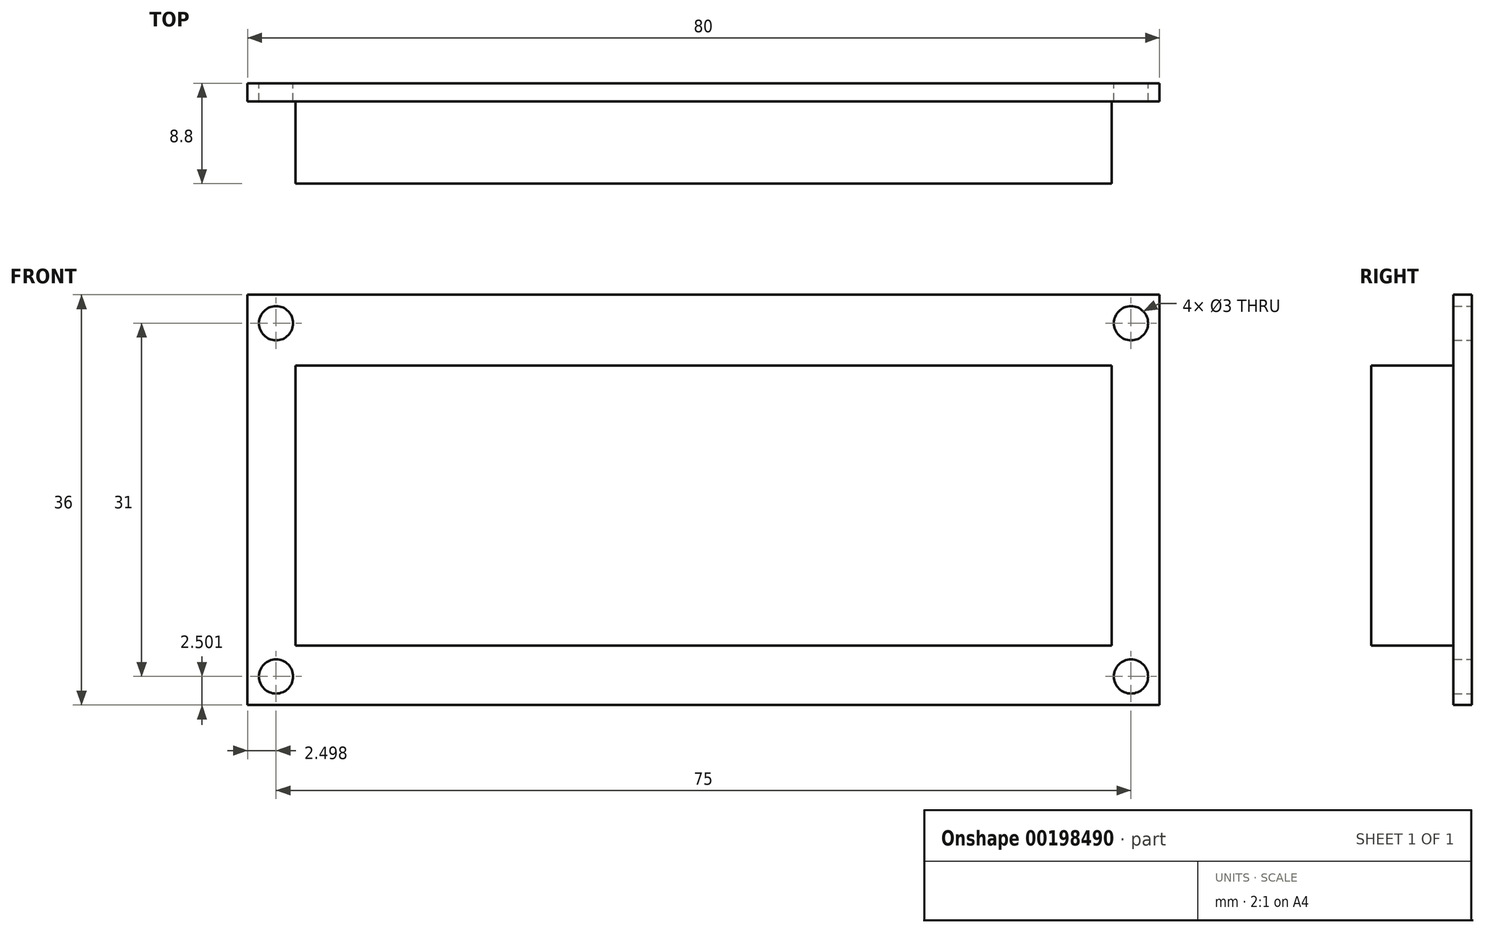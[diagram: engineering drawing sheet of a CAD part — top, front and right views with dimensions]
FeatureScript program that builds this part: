
annotation { "Feature Type Name" : "Feature", "Feature Type Description" : "" }
export const myFeature = defineFeature(function(context is Context, id is Id, definition is map)
    precondition{}
    {
        {
            var Q0;
            Q0=qCreatedBy(makeId("Front.planeOp"),FACE);
            var sketch = newSketch(context, id + "F0", { "sketchPlane" : qUnion([Q0])});
            skLineSegment(sketch, "E0.bottom", {"start": v(-37.3, 13.68) * mm, "end": v(42.7, 13.68) * mm});
            skLineSegment(sketch, "E0.top", {"start": v(-37.3, -22.32) * mm, "end": v(42.7, -22.32) * mm});
            skLineSegment(sketch, "E0.left", {"start": v(-37.3, 13.68) * mm, "end": v(-37.3, -22.32) * mm});
            skLineSegment(sketch, "E0.right", {"start": v(42.7, 13.68) * mm, "end": v(42.7, -22.32) * mm});
            skCircle(sketch, "E1", {"center": v(-34.8, 11.18) * mm, "radius": 1.5 * mm});
            skCircle(sketch, "E2", {"center": v(40.2, 11.18) * mm, "radius": 1.5 * mm});
            skCircle(sketch, "E3", {"center": v(40.2, -19.82) * mm, "radius": 1.5 * mm});
            skCircle(sketch, "E4", {"center": v(-34.8, -19.82) * mm, "radius": 1.5 * mm});
            skSolve(sketch);
        }
        {
            var Q0;
            Q0=makeQuery(id+"F0.imprint","IMPRINT",FACE,{"disambiguationData":[TD([[makeQuery(id+"F0.imprint","IMPRINT",EDGE,{"derivedFrom":sQuery(id+"F0.wireOp",EDGE,"E0.bottom")}),-1.0]])]});
            extrude(context, id + "F1", {"entities" : qUnion([Q0]), "depth" : 1.6 * mm});
        }
        {
            var Q0;
            Q0=makeQuery(id+"F1.opExtrude","CAP_FACE",FACE,{"disambiguationData":[OSD([sQuery(id+"F0.wireOp",EDGE,"E0.bottom"),sQuery(id+"F0.wireOp",EDGE,"E0.top"),sQuery(id+"F0.wireOp",EDGE,"E0.left"),sQuery(id+"F0.wireOp",EDGE,"E0.right"),sQuery(id+"F0.wireOp",EDGE,"E1"),sQuery(id+"F0.wireOp",EDGE,"E2"),sQuery(id+"F0.wireOp",EDGE,"E3"),sQuery(id+"F0.wireOp",EDGE,"E4")])],"isStart":false});
            var sketch = newSketch(context, id + "F2", { "sketchPlane" : qUnion([Q0])});
            skLineSegment(sketch, "E5.bottom", {"start": v(-33.1, 7.48) * mm, "end": v(38.5, 7.48) * mm});
            skLineSegment(sketch, "E5.top", {"start": v(-33.1, -17.12) * mm, "end": v(38.5, -17.12) * mm});
            skLineSegment(sketch, "E5.left", {"start": v(-33.1, 7.48) * mm, "end": v(-33.1, -17.12) * mm});
            skLineSegment(sketch, "E5.right", {"start": v(38.5, 7.48) * mm, "end": v(38.5, -17.12) * mm});
            skSolve(sketch);
        }
        {
            var Q0;
            Q0 = qSketchRegion(id + "F2", true);
            extrude(context, id + "F3", {"entities" : qUnion([Q0]), "operationType" : NewBodyOperationType.ADD, "depth" : 7.2 * mm});
        }
        {
            var Q0;
            Q0=makeQuery(id+"F3.opExtrude","CAP_FACE",FACE,{"disambiguationData":[OSD([sQuery(id+"F2.wireOp",EDGE,"E5.bottom"),sQuery(id+"F2.wireOp",EDGE,"E5.top"),sQuery(id+"F2.wireOp",EDGE,"E5.left"),sQuery(id+"F2.wireOp",EDGE,"E5.right")])],"isStart":false});
            var sketch = newSketch(context, id + "F4", { "sketchPlane" : qUnion([Q0])});
            skLineSegment(sketch, "E6.bottom", {"start": v(-29.75, 1.53) * mm, "end": v(35.25, 1.53) * mm});
            skLineSegment(sketch, "E6.top", {"start": v(-29.75, -12.47) * mm, "end": v(35.25, -12.47) * mm});
            skLineSegment(sketch, "E6.left", {"start": v(-29.75, 1.53) * mm, "end": v(-29.75, -12.47) * mm});
            skLineSegment(sketch, "E6.right", {"start": v(35.25, 1.53) * mm, "end": v(35.25, -12.47) * mm});
            skSolve(sketch);
        }
        {
            var Q0;
            Q0=makeQuery(id+"F4.imprint","IMPRINT",FACE,{"disambiguationData":[TD([[makeQuery(id+"F4.imprint","IMPRINT",EDGE,{"derivedFrom":sQuery(id+"F4.wireOp",EDGE,"E6.bottom")}),-1.0]])]});
            extrude(context, id + "F5", {"entities" : qUnion([Q0]), "operationType" : NewBodyOperationType.ADD, "oppositeDirection" : true, "depth" : 1 * mm});
        }
    });
